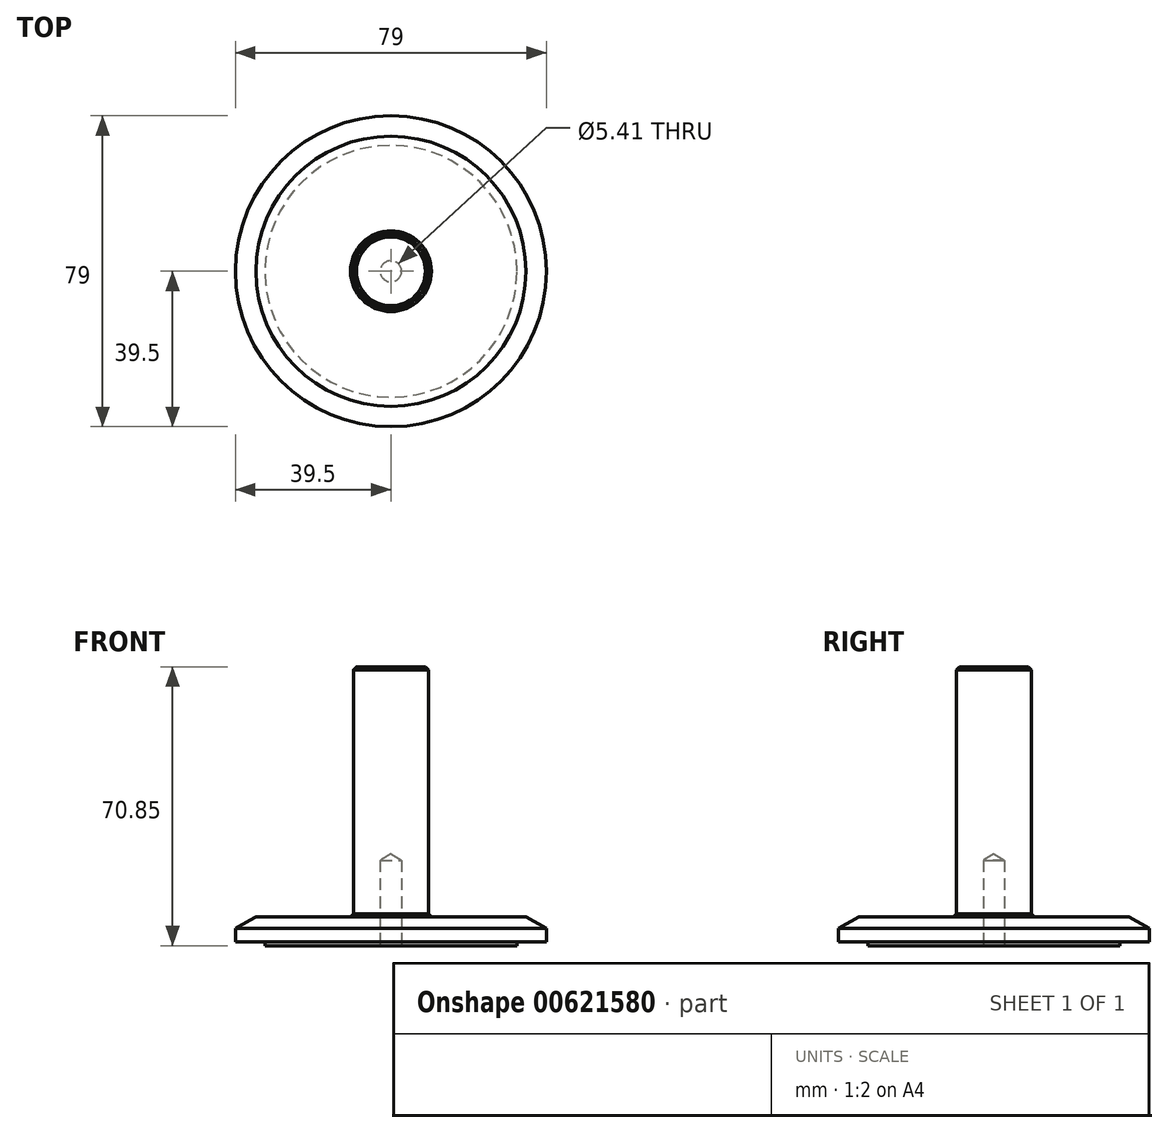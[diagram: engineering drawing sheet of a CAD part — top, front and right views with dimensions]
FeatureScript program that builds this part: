
annotation { "Feature Type Name" : "Feature", "Feature Type Description" : "" }
export const myFeature = defineFeature(function(context is Context, id is Id, definition is map)
    precondition{}
    {
        {
            var Q0;
            Q0=qCreatedBy(makeId("Front.planeOp"),FACE);
            var sketch = newSketch(context, id + "F0", { "sketchPlane" : qUnion([Q0])});
            skLineSegment(sketch, "E0", {"start": v(0, 0) * mm, "end": v(-32, 0) * mm});
            skLineSegment(sketch, "E1", {"start": v(-32, 0) * mm, "end": v(-32, 1) * mm});
            skLineSegment(sketch, "E2", {"start": v(-32, 1) * mm, "end": v(-39.5, 1) * mm});
            skLineSegment(sketch, "E3", {"start": v(-39.5, 1) * mm, "end": v(-39.5, 7.35) * mm});
            skLineSegment(sketch, "E4", {"start": v(-39.5, 7.35) * mm, "end": v(-9.5, 7.35) * mm});
            skLineSegment(sketch, "E5", {"start": v(-9.5, 7.35) * mm, "end": v(-9.5, 70.85) * mm});
            skLineSegment(sketch, "E6", {"start": v(-9.5, 70.85) * mm, "end": v(0, 70.85) * mm});
            skLineSegment(sketch, "E7", {"start": v(0, 70.85) * mm, "end": v(0, 0) * mm});
            skSolve(sketch);
        }
        {
            var Q0;
            Q0 = qSketchRegion(id + "F0", true);
            var Q1;
            Q1=sQuery(id+"F0.wireOp",EDGE,"E7");
            revolve(context, id + "F1", {"entities" : qUnion([Q0]), "axis" : qUnion([Q1]), "revolveType" : RevolveType.FULL});
        }
        {
            var Q0;
            Q0=makeQuery(id+"F1.opRevolve","SWEPT_EDGE",EDGE,{"disambiguationData":[OSD([sQuery(id+"F0.wireOp",EDGE,"E5"),sQuery(id+"F0.wireOp",EDGE,"E6")])]});
            var Q1;
            Q1=makeQuery(id+"F1.opRevolve","SWEPT_EDGE",EDGE,{"disambiguationData":[OSD([sQuery(id+"F0.wireOp",EDGE,"E4"),sQuery(id+"F0.wireOp",EDGE,"E5")])]});
            chamfer(context, id + "F2", {"entities" : qUnion([Q0, Q1]), "width" : .75 * mm, "tangentPropagation" : true});
        }
        {
            var Q0;
            Q0=makeQuery(id+"F1.opRevolve","SWEPT_EDGE",EDGE,{"disambiguationData":[OSD([sQuery(id+"F0.wireOp",EDGE,"E3"),sQuery(id+"F0.wireOp",EDGE,"E4")])]});
            chamfer(context, id + "F3", {"entities" : qUnion([Q0]), "chamferType" : ChamferType.OFFSET_ANGLE, "width" : 3 * mm, "oppositeDirection" : true, "angle" : 60 * degree, "tangentPropagation" : true});
        }
        {
            var Q0;
            Q0=makeQuery(id+"F1.opRevolve","SWEPT_FACE",FACE,{"disambiguationData":[OSD([sQuery(id+"F0.wireOp",EDGE,"E0")])]});
            var sketch = newSketch(context, id + "F4", { "sketchPlane" : qUnion([Q0])});
            skPoint(sketch, "E8", {"position": v(0, 0) * mm});
            skSolve(sketch);
        }
        {
            var Q0;
            Q0=sQuery(id+"F4.wireOp",VERTEX,"E8");
            var Q1;
            Q1=makeQuery(id+"F1.opRevolve","SWEPT_BODY",BODY,{"disambiguationData":[OSD([sQuery(id+"F0.wireOp",EDGE,"E0"),sQuery(id+"F0.wireOp",EDGE,"E1"),sQuery(id+"F0.wireOp",EDGE,"E2"),sQuery(id+"F0.wireOp",EDGE,"E3"),sQuery(id+"F0.wireOp",EDGE,"E4"),sQuery(id+"F0.wireOp",EDGE,"E5"),sQuery(id+"F0.wireOp",EDGE,"E6"),sQuery(id+"F0.wireOp",EDGE,"E7")])]});
            hole(context, id + "F5", {"style" : HoleStyle.SIMPLE, "endStyle" : HoleEndStyle.BLIND, "standardTappedOrClearance" : lookupTablePath({ "standard" : "ANSI", "engagement" : "75%", "pitch" : "28 tpi", "size" : "1/4", "type" : "Tapped" }), "standardBlindInLast" : lookupTablePath({ "standard" : "ANSI", "engagement" : "75%", "pitch" : "28 tpi", "size" : "1/4", "type" : "Tapped" }), "holeDiameter" : 5.4 * mm, "majorDiameter" : 6.35 * mm, "showTappedDepth" : true, "holeDepth" : 21.72 * mm, "tappedDepth" : 19 * mm, "tapClearance" : 3, "startFromSketch" : true, "locations" : qUnion([Q0]), "scope" : qUnion([Q1])});
        }
    });
